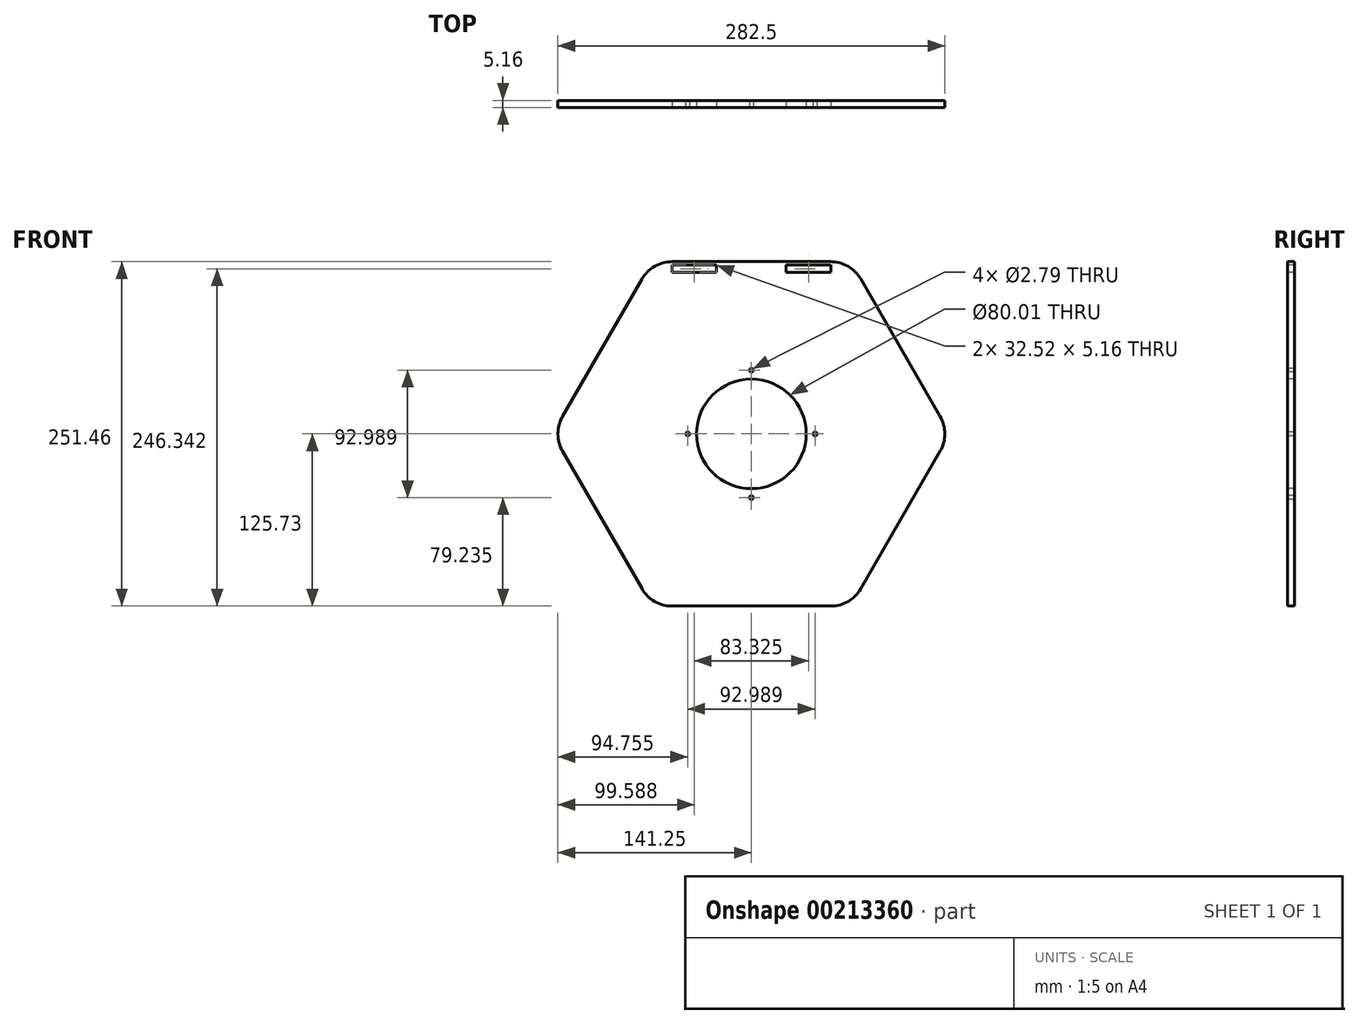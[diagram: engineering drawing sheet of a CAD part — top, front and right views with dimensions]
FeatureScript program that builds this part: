
annotation { "Feature Type Name" : "Feature", "Feature Type Description" : "" }
export const myFeature = defineFeature(function(context is Context, id is Id, definition is map)
    precondition{}
    {
        {
            var Q0;
            Q0=qCreatedBy(makeId("Front.planeOp"),FACE);
            var sketch = newSketch(context, id + "F0", { "sketchPlane" : qUnion([Q0])});
            skCircle(sketch, "E0.cCircle", {"center": v(0, 0) * mm, "radius": 125.73 * mm, "construction": true});
            skLineSegment(sketch, "E0.0", {"start": v(79.92, 113.03) * mm, "end": v(137.85, 12.7) * mm});
            skLineSegment(sketch, "E0.1", {"start": v(137.85, -12.7) * mm, "end": v(79.92, -113.03) * mm});
            skLineSegment(sketch, "E0.2", {"start": v(57.93, -125.73) * mm, "end": v(-57.93, -125.73) * mm});
            skLineSegment(sketch, "E0.3", {"start": v(-79.92, -113.03) * mm, "end": v(-137.85, -12.7) * mm});
            skLineSegment(sketch, "E0.4", {"start": v(-137.85, 12.7) * mm, "end": v(-79.92, 113.03) * mm});
            skLineSegment(sketch, "E0.5", {"start": v(-57.93, 125.73) * mm, "end": v(57.93, 125.73) * mm});
            skPoint(sketch, "E0.0.midPoint", {"position": v(108.89, 62.87) * mm});
            skPoint(sketch, "E1.visualSharp", {"position": v(-72.6, 125.73) * mm});
            skArc(sketch, "E1.filletArc", {"start": v(-57.93, 125.73) * mm, "mid": v(-70.63, 122.33) * mm, "end": v(-79.92, 113.03) * mm});
            skPoint(sketch, "E2.visualSharp", {"position": v(72.6, 125.73) * mm});
            skArc(sketch, "E2.filletArc", {"start": v(79.92, 113.03) * mm, "mid": v(70.63, 122.33) * mm, "end": v(57.93, 125.73) * mm});
            skPoint(sketch, "E3.visualSharp", {"position": v(145.18, 0) * mm});
            skArc(sketch, "E3.filletArc", {"start": v(137.85, -12.7) * mm, "mid": v(141.25, 0) * mm, "end": v(137.85, 12.7) * mm});
            skPoint(sketch, "E4.visualSharp", {"position": v(72.6, -125.73) * mm});
            skArc(sketch, "E4.filletArc", {"start": v(57.93, -125.73) * mm, "mid": v(70.63, -122.33) * mm, "end": v(79.92, -113.03) * mm});
            skPoint(sketch, "E5.visualSharp", {"position": v(-72.6, -125.73) * mm});
            skArc(sketch, "E5.filletArc", {"start": v(-79.92, -113.03) * mm, "mid": v(-70.63, -122.33) * mm, "end": v(-57.93, -125.73) * mm});
            skPoint(sketch, "E6.visualSharp", {"position": v(-145.18, 0) * mm});
            skArc(sketch, "E6.filletArc", {"start": v(-137.85, 12.7) * mm, "mid": v(-141.25, 0) * mm, "end": v(-137.85, -12.7) * mm});
            skSolve(sketch);
        }
        {
            var Q0;
            Q0=makeQuery(id+"F0.imprint","IMPRINT",FACE,{"disambiguationData":[TD([[makeQuery(id+"F0.imprint","IMPRINT",EDGE,{"derivedFrom":sQuery(id+"F0.wireOp",EDGE,"E0.0")}),-1.0]])]});
            extrude(context, id + "F1", {"entities" : qUnion([Q0]), "oppositeDirection" : true, "depth" : 5.16 * mm});
        }
        {
            var Q0;
            Q0=makeQuery(id+"F1.opExtrude","CAP_FACE",FACE,{"disambiguationData":[OSD([sQuery(id+"F0.wireOp",EDGE,"E0.0"),sQuery(id+"F0.wireOp",EDGE,"E0.1"),sQuery(id+"F0.wireOp",EDGE,"E0.2"),sQuery(id+"F0.wireOp",EDGE,"E0.3"),sQuery(id+"F0.wireOp",EDGE,"E0.4"),sQuery(id+"F0.wireOp",EDGE,"E0.5"),sQuery(id+"F0.wireOp",EDGE,"E1.filletArc"),sQuery(id+"F0.wireOp",EDGE,"E2.filletArc"),sQuery(id+"F0.wireOp",EDGE,"E3.filletArc"),sQuery(id+"F0.wireOp",EDGE,"E4.filletArc"),sQuery(id+"F0.wireOp",EDGE,"E5.filletArc"),sQuery(id+"F0.wireOp",EDGE,"E6.filletArc")])],"isStart":true});
            var sketch = newSketch(context, id + "F2", { "sketchPlane" : qUnion([Q0])});
            skCircle(sketch, "E7", {"center": v(0, 0) * mm, "radius": 40 * mm});
            skCircle(sketch, "E8", {"center": v(0, 0) * mm, "radius": 46.5 * mm, "construction": true});
            skCircle(sketch, "E9", {"center": v(0, 0) * mm, "radius": 51.75 * mm, "construction": true});
            skCircle(sketch, "E10", {"center": v(0, 46.5) * mm, "radius": 1.4 * mm});
            skCircle(sketch, "E11.1.0", {"center": v(-46.5, 0) * mm, "radius": 1.4 * mm});
            skCircle(sketch, "E11.2.0", {"center": v(0, -46.5) * mm, "radius": 1.4 * mm});
            skCircle(sketch, "E11.3.0", {"center": v(46.5, 0) * mm, "radius": 1.4 * mm});
            skSolve(sketch);
        }
        {
            var Q0;
            Q0=qSketchRegion(id+"F2",true);
            extrude(context, id + "F3", {"entities" : qUnion([Q0]), "operationType" : NewBodyOperationType.REMOVE, "endBound" : BoundingType.THROUGH_ALL, "oppositeDirection" : true, "depth" : 25.4 * mm});
        }
        {
            var Q0;
            Q0=makeQuery(id+"F1.opExtrude","CAP_FACE",FACE,{"disambiguationData":[OSD([sQuery(id+"F0.wireOp",EDGE,"E0.0"),sQuery(id+"F0.wireOp",EDGE,"E0.1"),sQuery(id+"F0.wireOp",EDGE,"E0.2"),sQuery(id+"F0.wireOp",EDGE,"E0.3"),sQuery(id+"F0.wireOp",EDGE,"E0.4"),sQuery(id+"F0.wireOp",EDGE,"E0.5"),sQuery(id+"F0.wireOp",EDGE,"E1.filletArc"),sQuery(id+"F0.wireOp",EDGE,"E2.filletArc"),sQuery(id+"F0.wireOp",EDGE,"E3.filletArc"),sQuery(id+"F0.wireOp",EDGE,"E4.filletArc"),sQuery(id+"F0.wireOp",EDGE,"E5.filletArc"),sQuery(id+"F0.wireOp",EDGE,"E6.filletArc")])],"isStart":true});
            var sketch = newSketch(context, id + "F4", { "sketchPlane" : qUnion([Q0])});
            skLineSegment(sketch, "E12.bottom", {"start": v(-57.92, 123.19) * mm, "end": v(57.92, 123.19) * mm});
            skLineSegment(sketch, "E12.top", {"start": v(-57.92, 118.03) * mm, "end": v(57.92, 118.03) * mm});
            skLineSegment(sketch, "E12.left", {"start": v(-57.92, 123.19) * mm, "end": v(-57.92, 118.03) * mm});
            skLineSegment(sketch, "E12.right", {"start": v(57.92, 123.19) * mm, "end": v(57.92, 118.03) * mm});
            skPoint(sketch, "E13", {"position": v(0, 123.19) * mm});
            skPoint(sketch, "E14", {"position": v(0, 125.73) * mm});
            skLineSegment(sketch, "E15.bottom", {"start": v(-25.4, 123.19) * mm, "end": v(25.4, 123.19) * mm});
            skLineSegment(sketch, "E15.top", {"start": v(-25.4, 118.03) * mm, "end": v(25.4, 118.03) * mm});
            skLineSegment(sketch, "E15.left", {"start": v(-25.4, 123.19) * mm, "end": v(-25.4, 118.03) * mm});
            skLineSegment(sketch, "E15.right", {"start": v(25.4, 123.19) * mm, "end": v(25.4, 118.03) * mm});
            skSolve(sketch);
        }
        {
            var Q0;
            {var subQ0=sQuery(id+"F4.wireOp",EDGE,"E12.left");Q0=makeQuery(id+"F4.imprint","IMPRINT",FACE,{"disambiguationData":[TD([[makeQuery(id+"F4.imprint","IMPRINT",EDGE,{"derivedFrom":subQ0}),1.0]])]});}
            var Q1;
            {var subQ0=sQuery(id+"F4.wireOp",EDGE,"E12.right");Q1=makeQuery(id+"F4.imprint","IMPRINT",FACE,{"disambiguationData":[TD([[makeQuery(id+"F4.imprint","IMPRINT",EDGE,{"derivedFrom":subQ0}),-1.0]])]});}
            extrude(context, id + "F5", {"entities" : qUnion([Q0, Q1]), "operationType" : NewBodyOperationType.REMOVE, "endBound" : BoundingType.THROUGH_ALL, "oppositeDirection" : true, "depth" : 25.4 * mm});
        }
        {
            var Q0;
            Q0=qCreatedBy(makeId("Right.planeOp"),FACE);
            var sketch = newSketch(context, id + "F6", { "sketchPlane" : qUnion([Q0])});
            skLineSegment(sketch, "E16", {"start": v(0, 0) * mm, "end": v(-137.26, 0) * mm, "construction": true});
            skSolve(sketch);
        }
    });
